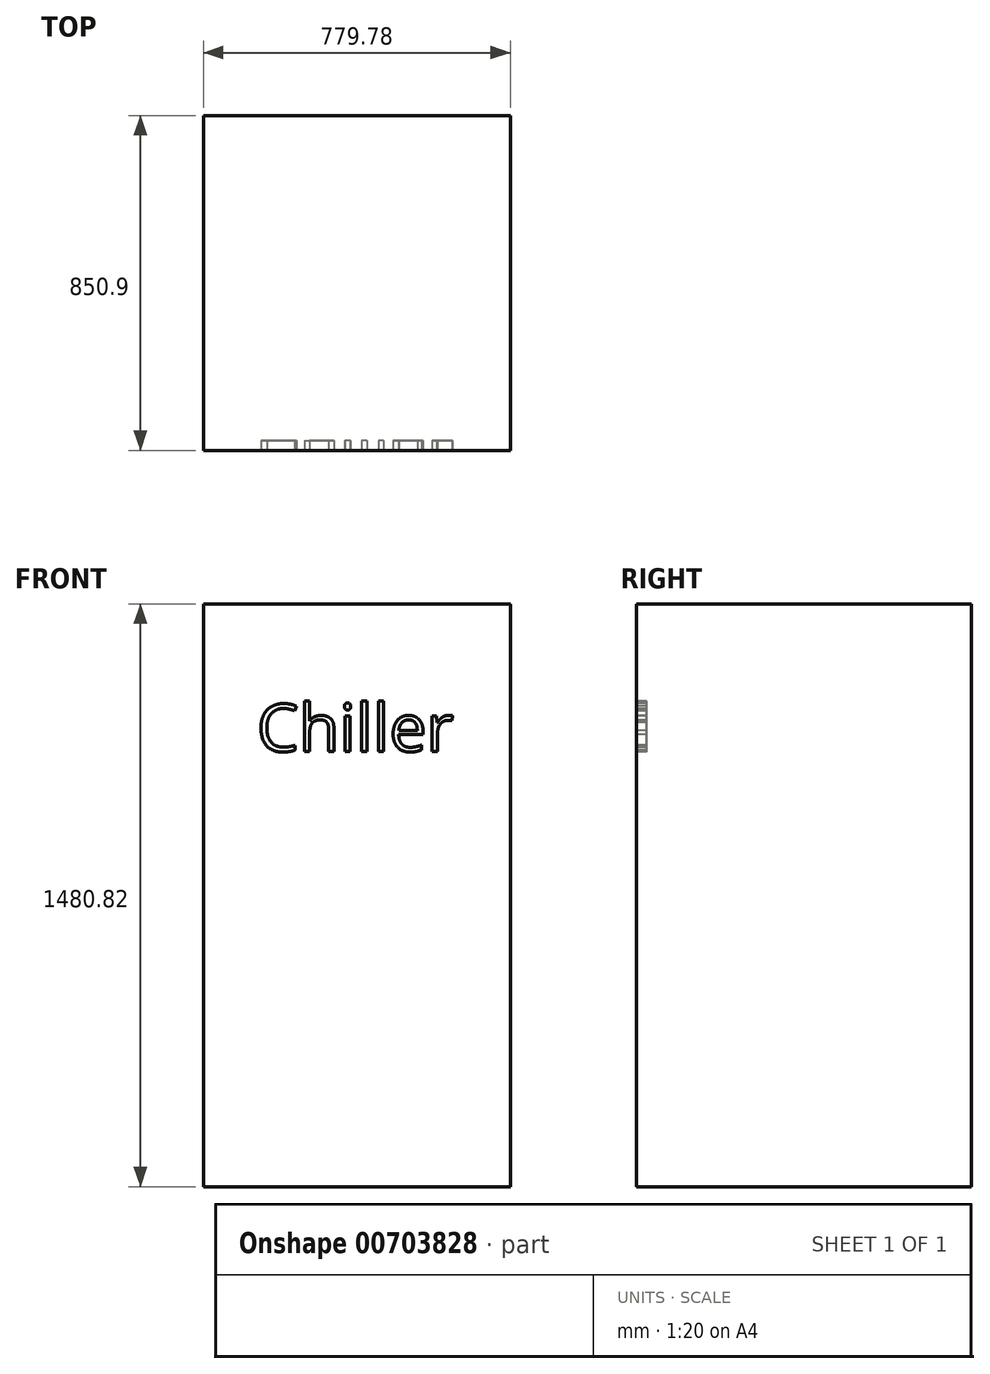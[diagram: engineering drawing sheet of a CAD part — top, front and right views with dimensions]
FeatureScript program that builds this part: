
annotation { "Feature Type Name" : "Feature", "Feature Type Description" : "" }
export const myFeature = defineFeature(function(context is Context, id is Id, definition is map)
    precondition{}
    {
        {
            var Q0;
            Q0=qCreatedBy(makeId("Top.planeOp"),FACE);
            var sketch = newSketch(context, id + "F0", { "sketchPlane" : qUnion([Q0])});
            skLineSegment(sketch, "E0.bottom", {"start": v(389.9, -425.45) * mm, "end": v(-389.9, -425.45) * mm});
            skLineSegment(sketch, "E0.top", {"start": v(389.9, 425.45) * mm, "end": v(-389.9, 425.45) * mm});
            skLineSegment(sketch, "E0.left", {"start": v(389.9, -425.45) * mm, "end": v(389.9, 425.45) * mm});
            skLineSegment(sketch, "E0.right", {"start": v(-389.9, -425.45) * mm, "end": v(-389.9, 425.45) * mm});
            skPoint(sketch, "E0.middle", {"position": v(0, 0) * mm});
            skSolve(sketch);
        }
        {
            var Q0;
            Q0=qSketchRegion(id+"F0",true);
            extrude(context, id + "F1", {"entities" : qUnion([Q0]), "depth" : 1480.82 * mm, "offsetDistance" : 25.4 * mm});
        }
        {
            var Q0;
            Q0=makeQuery(id+"F1.opExtrude","SWEPT_FACE",FACE,{"disambiguationData":[OSD([sQuery(id+"F0.wireOp",EDGE,"E0.bottom")])]});
            var sketch = newSketch(context, id + "F2", { "sketchPlane" : qUnion([Q0])});
            skText(sketch, "E1", { "text": "Chiller", "fontName": "OpenSans-Regular.ttf"});
            const initialGuessF2  = {"E1": [-0.254, 1.10585, 1, 0, 0.12097]};
            skSetInitialGuess(sketch, initialGuessF2);
            skSolve(sketch);
        }
        {
            var Q0;
            Q0=qSketchRegion(id+"F2",true);
            extrude(context, id + "F3", {"entities" : qUnion([Q0]), "operationType" : NewBodyOperationType.REMOVE, "oppositeDirection" : true, "depth" : 25.4 * mm, "offsetDistance" : 25.4 * mm});
        }
    });
